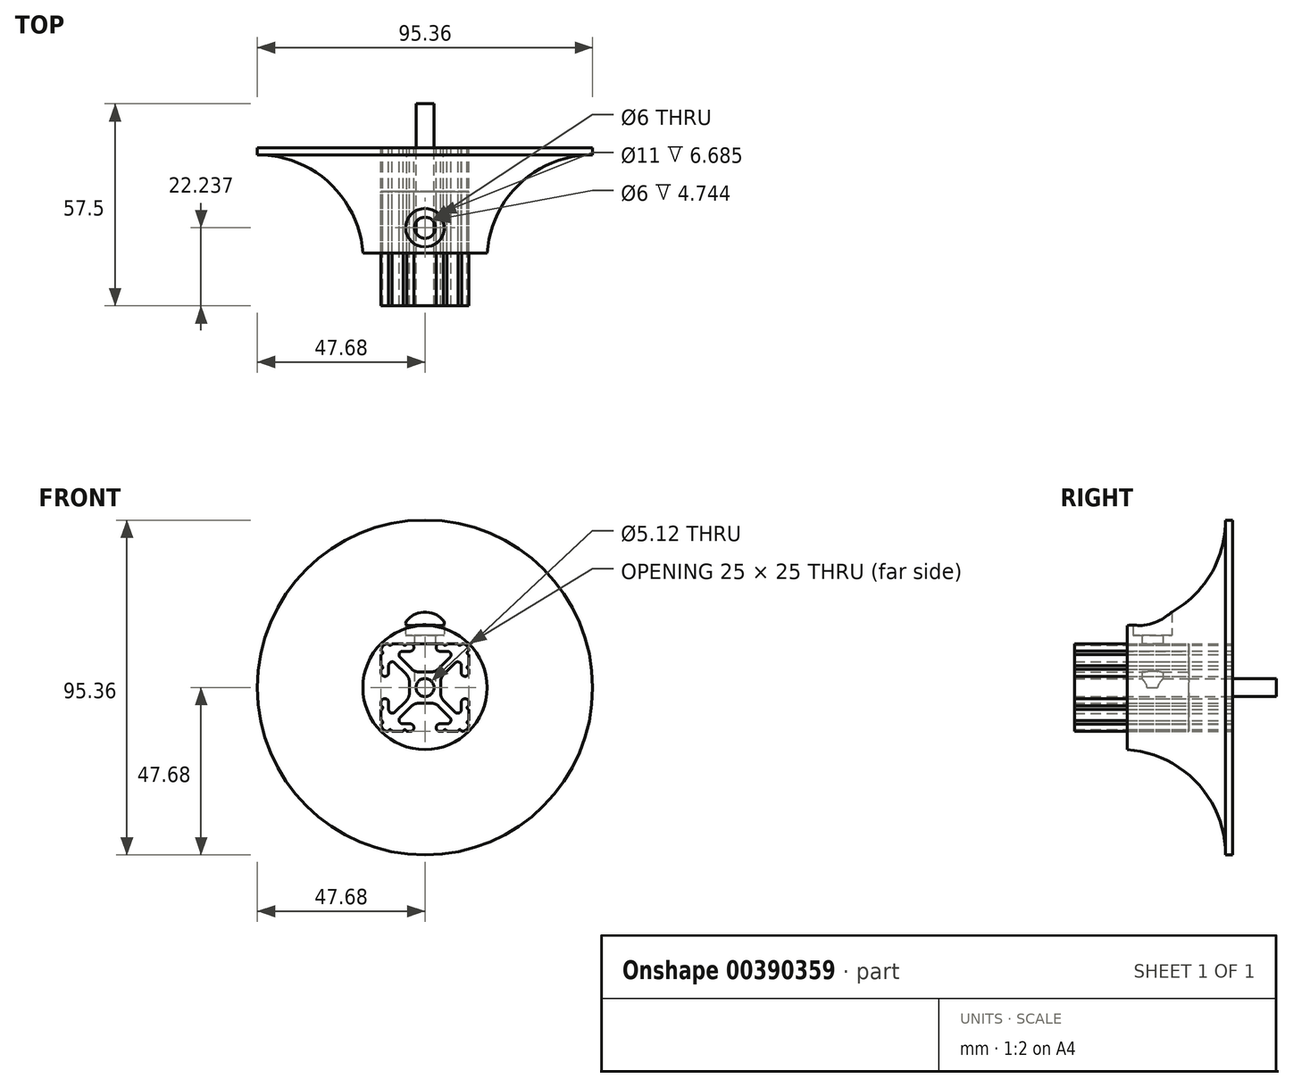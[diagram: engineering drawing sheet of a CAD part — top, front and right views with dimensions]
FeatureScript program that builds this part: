
annotation { "Feature Type Name" : "Feature", "Feature Type Description" : "" }
export const myFeature = defineFeature(function(context is Context, id is Id, definition is map)
    precondition{}
    {
        {
            var Q0;
            Q0=qCreatedBy(makeId("Front.planeOp"),FACE);
            var sketch = newSketch(context, id + "F0", { "sketchPlane" : qUnion([Q0])});
            skCircle(sketch, "E0", {"center": v(0, 0) * mm, "radius": 2.56 * mm});
            skArc(sketch, "E1", {"start": v(-1.68, -4.43) * mm, "mid": v(-2.88, -4.66) * mm, "end": v(-3.9, -5.34) * mm});
            skLineSegment(sketch, "E2", {"start": v(-1.68, -4.42) * mm, "end": v(1.68, -4.42) * mm});
            skArc(sketch, "E3", {"start": v(3.9, -5.34) * mm, "mid": v(2.88, -4.66) * mm, "end": v(1.68, -4.43) * mm});
            skLineSegment(sketch, "E4", {"start": v(3.9, -5.34) * mm, "end": v(7.07, -8.5) * mm});
            skArc(sketch, "E5", {"start": v(6.32, -10.32) * mm, "mid": v(7.3, -9.67) * mm, "end": v(7.07, -8.5) * mm});
            skLineSegment(sketch, "E6", {"start": v(6.32, -10.33) * mm, "end": v(4.22, -10.33) * mm});
            skArc(sketch, "E7", {"start": v(4.22, -10.32) * mm, "mid": v(3.49, -10.63) * mm, "end": v(3.19, -11.36) * mm});
            skLineSegment(sketch, "E8", {"start": v(3.19, -11.36) * mm, "end": v(3.19, -11.47) * mm});
            skArc(sketch, "E9", {"start": v(3.19, -11.47) * mm, "mid": v(3.49, -12.2) * mm, "end": v(4.22, -12.5) * mm});
            skLineSegment(sketch, "E10", {"start": v(4.22, -12.5) * mm, "end": v(5.23, -12.5) * mm});
            skArc(sketch, "E11", {"start": v(6.23, -12.5) * mm, "mid": v(5.73, -12) * mm, "end": v(5.23, -12.5) * mm});
            skLineSegment(sketch, "E12", {"start": v(6.23, -12.5) * mm, "end": v(9.4, -12.5) * mm});
            skArc(sketch, "E13", {"start": v(10.4, -12.5) * mm, "mid": v(9.9, -12) * mm, "end": v(9.4, -12.5) * mm});
            skArc(sketch, "E14", {"start": v(10.4, -12.5) * mm, "mid": v(11.9, -11.9) * mm, "end": v(12.5, -10.4) * mm});
            skArc(sketch, "E15", {"start": v(12.5, -9.4) * mm, "mid": v(12, -9.9) * mm, "end": v(12.5, -10.4) * mm});
            skLineSegment(sketch, "E16", {"start": v(12.5, -9.4) * mm, "end": v(12.5, -6.23) * mm});
            skArc(sketch, "E17", {"start": v(12.5, -5.23) * mm, "mid": v(12, -5.73) * mm, "end": v(12.5, -6.23) * mm});
            skLineSegment(sketch, "E18", {"start": v(12.5, -5.23) * mm, "end": v(12.5, -4.22) * mm});
            skArc(sketch, "E19", {"start": v(12.5, -4.22) * mm, "mid": v(12.2, -3.49) * mm, "end": v(11.47, -3.19) * mm});
            skLineSegment(sketch, "E20", {"start": v(11.47, -3.19) * mm, "end": v(11.36, -3.19) * mm});
            skArc(sketch, "E21", {"start": v(11.36, -3.19) * mm, "mid": v(10.63, -3.49) * mm, "end": v(10.32, -4.22) * mm});
            skLineSegment(sketch, "E22", {"start": v(10.33, -4.22) * mm, "end": v(10.33, -6.3) * mm});
            skArc(sketch, "E23", {"start": v(8.6, -7.02) * mm, "mid": v(9.7, -7.24) * mm, "end": v(10.33, -6.3) * mm});
            skLineSegment(sketch, "E24", {"start": v(8.6, -7.02) * mm, "end": v(5.36, -3.78) * mm});
            skArc(sketch, "E25", {"start": v(4.44, -1.57) * mm, "mid": v(4.68, -2.77) * mm, "end": v(5.36, -3.78) * mm});
            skLineSegment(sketch, "E26", {"start": v(4.44, -1.57) * mm, "end": v(4.44, 1.57) * mm});
            skArc(sketch, "E27", {"start": v(5.36, 3.78) * mm, "mid": v(4.68, 2.77) * mm, "end": v(4.44, 1.57) * mm});
            skLineSegment(sketch, "E28", {"start": v(5.36, 3.78) * mm, "end": v(8.6, 7.02) * mm});
            skArc(sketch, "E29", {"start": v(10.33, 6.3) * mm, "mid": v(9.7, 7.24) * mm, "end": v(8.6, 7.02) * mm});
            skLineSegment(sketch, "E30", {"start": v(10.33, 6.3) * mm, "end": v(10.33, 4.22) * mm});
            skArc(sketch, "E31", {"start": v(10.32, 4.22) * mm, "mid": v(10.63, 3.49) * mm, "end": v(11.36, 3.19) * mm});
            skLineSegment(sketch, "E32", {"start": v(11.36, 3.19) * mm, "end": v(11.47, 3.19) * mm});
            skArc(sketch, "E33", {"start": v(11.47, 3.19) * mm, "mid": v(12.2, 3.49) * mm, "end": v(12.5, 4.22) * mm});
            skLineSegment(sketch, "E34", {"start": v(12.5, 4.22) * mm, "end": v(12.5, 5.23) * mm});
            skArc(sketch, "E35", {"start": v(12.5, 6.23) * mm, "mid": v(12, 5.73) * mm, "end": v(12.5, 5.23) * mm});
            skLineSegment(sketch, "E36", {"start": v(12.5, 6.23) * mm, "end": v(12.5, 9.4) * mm});
            skArc(sketch, "E37", {"start": v(12.5, 10.4) * mm, "mid": v(12, 9.9) * mm, "end": v(12.5, 9.4) * mm});
            skArc(sketch, "E38", {"start": v(12.5, 10.4) * mm, "mid": v(11.9, 11.9) * mm, "end": v(10.4, 12.5) * mm});
            skArc(sketch, "E39", {"start": v(9.4, 12.5) * mm, "mid": v(9.9, 12) * mm, "end": v(10.4, 12.5) * mm});
            skLineSegment(sketch, "E40", {"start": v(9.4, 12.5) * mm, "end": v(6.23, 12.5) * mm});
            skArc(sketch, "E41", {"start": v(5.23, 12.5) * mm, "mid": v(5.73, 12) * mm, "end": v(6.23, 12.5) * mm});
            skLineSegment(sketch, "E42", {"start": v(5.23, 12.5) * mm, "end": v(4.22, 12.5) * mm});
            skArc(sketch, "E43", {"start": v(4.22, 12.5) * mm, "mid": v(3.49, 12.2) * mm, "end": v(3.19, 11.47) * mm});
            skLineSegment(sketch, "E44", {"start": v(3.19, 11.47) * mm, "end": v(3.19, 11.36) * mm});
            skArc(sketch, "E45", {"start": v(3.19, 11.36) * mm, "mid": v(3.49, 10.63) * mm, "end": v(4.22, 10.32) * mm});
            skLineSegment(sketch, "E46", {"start": v(4.22, 10.33) * mm, "end": v(6.37, 10.33) * mm});
            skArc(sketch, "E47", {"start": v(7.1, 8.59) * mm, "mid": v(7.32, 9.7) * mm, "end": v(6.37, 10.32) * mm});
            skLineSegment(sketch, "E48", {"start": v(7.1, 8.59) * mm, "end": v(3.84, 5.34) * mm});
            skArc(sketch, "E49", {"start": v(1.63, 4.43) * mm, "mid": v(2.82, 4.66) * mm, "end": v(3.84, 5.34) * mm});
            skLineSegment(sketch, "E50", {"start": v(1.63, 4.42) * mm, "end": v(-1.63, 4.42) * mm});
            skArc(sketch, "E51", {"start": v(-3.84, 5.34) * mm, "mid": v(-2.82, 4.66) * mm, "end": v(-1.63, 4.43) * mm});
            skLineSegment(sketch, "E52", {"start": v(-3.84, 5.34) * mm, "end": v(-7.1, 8.59) * mm});
            skArc(sketch, "E53", {"start": v(-6.37, 10.32) * mm, "mid": v(-7.32, 9.7) * mm, "end": v(-7.1, 8.59) * mm});
            skLineSegment(sketch, "E54", {"start": v(-6.37, 10.33) * mm, "end": v(-4.22, 10.33) * mm});
            skArc(sketch, "E55", {"start": v(-4.22, 10.32) * mm, "mid": v(-3.49, 10.63) * mm, "end": v(-3.19, 11.36) * mm});
            skLineSegment(sketch, "E56", {"start": v(-3.19, 11.36) * mm, "end": v(-3.19, 11.47) * mm});
            skArc(sketch, "E57", {"start": v(-3.19, 11.47) * mm, "mid": v(-3.49, 12.2) * mm, "end": v(-4.22, 12.5) * mm});
            skLineSegment(sketch, "E58", {"start": v(-4.22, 12.5) * mm, "end": v(-5.23, 12.5) * mm});
            skArc(sketch, "E59", {"start": v(-6.23, 12.5) * mm, "mid": v(-5.73, 12) * mm, "end": v(-5.23, 12.5) * mm});
            skLineSegment(sketch, "E60", {"start": v(-6.23, 12.5) * mm, "end": v(-9.4, 12.5) * mm});
            skArc(sketch, "E61", {"start": v(-10.4, 12.5) * mm, "mid": v(-9.9, 12) * mm, "end": v(-9.4, 12.5) * mm});
            skArc(sketch, "E62", {"start": v(-10.4, 12.5) * mm, "mid": v(-11.9, 11.9) * mm, "end": v(-12.5, 10.4) * mm});
            skArc(sketch, "E63", {"start": v(-12.5, 9.4) * mm, "mid": v(-12, 9.9) * mm, "end": v(-12.5, 10.4) * mm});
            skLineSegment(sketch, "E64", {"start": v(-12.5, 9.4) * mm, "end": v(-12.5, 6.23) * mm});
            skArc(sketch, "E65", {"start": v(-12.5, 5.23) * mm, "mid": v(-12, 5.73) * mm, "end": v(-12.5, 6.23) * mm});
            skLineSegment(sketch, "E66", {"start": v(-12.5, 5.23) * mm, "end": v(-12.5, 4.22) * mm});
            skArc(sketch, "E67", {"start": v(-12.5, 4.22) * mm, "mid": v(-12.2, 3.49) * mm, "end": v(-11.47, 3.19) * mm});
            skLineSegment(sketch, "E68", {"start": v(-11.47, 3.19) * mm, "end": v(-11.36, 3.19) * mm});
            skArc(sketch, "E69", {"start": v(-11.36, 3.19) * mm, "mid": v(-10.63, 3.49) * mm, "end": v(-10.32, 4.22) * mm});
            skLineSegment(sketch, "E70", {"start": v(-10.33, 4.22) * mm, "end": v(-10.33, 6.3) * mm});
            skArc(sketch, "E71", {"start": v(-8.6, 7.02) * mm, "mid": v(-9.7, 7.24) * mm, "end": v(-10.33, 6.3) * mm});
            skLineSegment(sketch, "E72", {"start": v(-8.6, 7.02) * mm, "end": v(-5.36, 3.78) * mm});
            skArc(sketch, "E73", {"start": v(-4.44, 1.57) * mm, "mid": v(-4.68, 2.77) * mm, "end": v(-5.36, 3.78) * mm});
            skLineSegment(sketch, "E74", {"start": v(-4.44, 1.57) * mm, "end": v(-4.44, -1.57) * mm});
            skArc(sketch, "E75", {"start": v(-5.36, -3.78) * mm, "mid": v(-4.68, -2.77) * mm, "end": v(-4.44, -1.57) * mm});
            skLineSegment(sketch, "E76", {"start": v(-5.36, -3.78) * mm, "end": v(-8.6, -7.02) * mm});
            skArc(sketch, "E77", {"start": v(-10.33, -6.3) * mm, "mid": v(-9.7, -7.24) * mm, "end": v(-8.6, -7.02) * mm});
            skLineSegment(sketch, "E78", {"start": v(-10.33, -6.3) * mm, "end": v(-10.33, -4.22) * mm});
            skArc(sketch, "E79", {"start": v(-10.32, -4.22) * mm, "mid": v(-10.63, -3.49) * mm, "end": v(-11.36, -3.19) * mm});
            skLineSegment(sketch, "E80", {"start": v(-11.36, -3.19) * mm, "end": v(-11.47, -3.19) * mm});
            skArc(sketch, "E81", {"start": v(-11.47, -3.19) * mm, "mid": v(-12.2, -3.49) * mm, "end": v(-12.5, -4.22) * mm});
            skLineSegment(sketch, "E82", {"start": v(-12.5, -4.22) * mm, "end": v(-12.5, -5.23) * mm});
            skArc(sketch, "E83", {"start": v(-12.5, -6.23) * mm, "mid": v(-12, -5.73) * mm, "end": v(-12.5, -5.23) * mm});
            skLineSegment(sketch, "E84", {"start": v(-12.5, -6.23) * mm, "end": v(-12.5, -9.4) * mm});
            skArc(sketch, "E85", {"start": v(-12.5, -10.4) * mm, "mid": v(-12, -9.9) * mm, "end": v(-12.5, -9.4) * mm});
            skArc(sketch, "E86", {"start": v(-12.5, -10.4) * mm, "mid": v(-11.9, -11.9) * mm, "end": v(-10.4, -12.5) * mm});
            skArc(sketch, "E87", {"start": v(-9.4, -12.5) * mm, "mid": v(-9.9, -12) * mm, "end": v(-10.4, -12.5) * mm});
            skLineSegment(sketch, "E88", {"start": v(-9.4, -12.5) * mm, "end": v(-6.23, -12.5) * mm});
            skArc(sketch, "E89", {"start": v(-5.23, -12.5) * mm, "mid": v(-5.73, -12) * mm, "end": v(-6.23, -12.5) * mm});
            skLineSegment(sketch, "E90", {"start": v(-5.23, -12.5) * mm, "end": v(-4.22, -12.5) * mm});
            skArc(sketch, "E91", {"start": v(-4.22, -12.5) * mm, "mid": v(-3.49, -12.2) * mm, "end": v(-3.19, -11.47) * mm});
            skLineSegment(sketch, "E92", {"start": v(-3.19, -11.47) * mm, "end": v(-3.19, -11.36) * mm});
            skArc(sketch, "E93", {"start": v(-3.19, -11.36) * mm, "mid": v(-3.49, -10.63) * mm, "end": v(-4.22, -10.32) * mm});
            skLineSegment(sketch, "E94", {"start": v(-4.22, -10.33) * mm, "end": v(-6.32, -10.33) * mm});
            skArc(sketch, "E95", {"start": v(-7.07, -8.5) * mm, "mid": v(-7.3, -9.67) * mm, "end": v(-6.32, -10.32) * mm});
            skLineSegment(sketch, "E96", {"start": v(-7.07, -8.5) * mm, "end": v(-3.9, -5.34) * mm});
            skSolve(sketch);
        }
        {
            var Q0;
            Q0=qCreatedBy(makeId("Front.planeOp"),FACE);
            var sketch = newSketch(context, id + "F1", { "sketchPlane" : qUnion([Q0])});
            skCircle(sketch, "E97", {"center": v(0, 0) * mm, "radius": 17.68 * mm});
            skCircle(sketch, "E98", {"center": v(0, 0) * mm, "radius": 47.67 * mm});
            skSolve(sketch);
        }
        {
            var Q0;
            Q0=qSketchRegion(id+"F1",true);
            var Q1;
            Q1=makeQuery(id+"F1.imprint","IMPRINT",FACE,{"disambiguationData":[TD([[makeQuery(id+"F1.imprint","IMPRINT",EDGE,{"derivedFrom":sQuery(id+"F1.wireOp",EDGE,"E97")}),1.0]])]});
            extrude(context, id + "F2", {"entities" : qUnion([Q0, Q1]), "depth" : 2 * mm});
        }
        {
            var Q0;
            Q0=makeQuery(id+"F1.imprint","IMPRINT",FACE,{"disambiguationData":[TD([[makeQuery(id+"F1.imprint","IMPRINT",EDGE,{"derivedFrom":sQuery(id+"F1.wireOp",EDGE,"E97")}),1.0]])]});
            extrude(context, id + "F3", {"entities" : qUnion([Q0]), "operationType" : NewBodyOperationType.ADD, "depth" : 30 * mm});
        }
        {
            var Q0;
            Q0=makeQuery(id+"F3.boolean.opBoolean","INTERSECT",EDGE,{"derivedFrom":[makeQuery(id+"F2.opExtrude","CAP_FACE",FACE,{"disambiguationData":[OSD([sQuery(id+"F1.wireOp",EDGE,"E98")])],"isStart":false}),makeQuery(id+"F3.opExtrude","SWEPT_FACE",FACE,{"disambiguationData":[OSD([sQuery(id+"F1.wireOp",EDGE,"E97")])]})]});
            fillet(context, id + "F4", {"entities" : qUnion([Q0]), "radius" : 30 * mm, "tangentPropagation" : true, "allowEdgeOverflow" : false});
        }
        {
            var Q0;
            Q0=makeQuery(id+"F1.imprint","IMPRINT",FACE,{"disambiguationData":[TD([[makeQuery(id+"F1.imprint","IMPRINT",EDGE,{"derivedFrom":sQuery(id+"F1.wireOp",EDGE,"E97")}),-1.0]])]});
            var sketch = newSketch(context, id + "F5", { "sketchPlane" : qUnion([Q0])});
            skArc(sketch, "E99.0.0", {"start": v(-6.32, -10.32) * mm, "mid": v(-7.3, -9.67) * mm, "end": v(-7.07, -8.5) * mm});
            skLineSegment(sketch, "E99.0.1", {"start": v(-7.07, -8.5) * mm, "end": v(-3.9, -5.34) * mm});
            skArc(sketch, "E99.0.2", {"start": v(-3.9, -5.34) * mm, "mid": v(-2.88, -4.66) * mm, "end": v(-1.68, -4.43) * mm});
            skLineSegment(sketch, "E99.0.3", {"start": v(-1.68, -4.42) * mm, "end": v(1.68, -4.42) * mm});
            skArc(sketch, "E99.0.4", {"start": v(1.68, -4.43) * mm, "mid": v(2.88, -4.66) * mm, "end": v(3.9, -5.34) * mm});
            skLineSegment(sketch, "E99.0.5", {"start": v(3.9, -5.34) * mm, "end": v(7.07, -8.5) * mm});
            skArc(sketch, "E99.0.6", {"start": v(7.07, -8.5) * mm, "mid": v(7.3, -9.67) * mm, "end": v(6.32, -10.33) * mm});
            skLineSegment(sketch, "E99.0.7", {"start": v(6.32, -10.33) * mm, "end": v(4.22, -10.33) * mm});
            skArc(sketch, "E99.0.8", {"start": v(4.22, -10.32) * mm, "mid": v(3.49, -10.63) * mm, "end": v(3.19, -11.36) * mm});
            skLineSegment(sketch, "E99.0.9", {"start": v(3.19, -11.36) * mm, "end": v(3.19, -11.47) * mm});
            skArc(sketch, "E99.0.10", {"start": v(3.19, -11.47) * mm, "mid": v(3.49, -12.2) * mm, "end": v(4.22, -12.5) * mm});
            skLineSegment(sketch, "E99.0.11", {"start": v(4.22, -12.5) * mm, "end": v(5.23, -12.5) * mm});
            skArc(sketch, "E99.0.12", {"start": v(5.23, -12.5) * mm, "mid": v(5.73, -12) * mm, "end": v(6.23, -12.5) * mm});
            skLineSegment(sketch, "E99.0.13", {"start": v(6.23, -12.5) * mm, "end": v(9.4, -12.5) * mm});
            skArc(sketch, "E99.0.14", {"start": v(9.4, -12.5) * mm, "mid": v(9.9, -12) * mm, "end": v(10.4, -12.5) * mm});
            skArc(sketch, "E99.0.15", {"start": v(10.4, -12.5) * mm, "mid": v(11.9, -11.9) * mm, "end": v(12.5, -10.4) * mm});
            skArc(sketch, "E99.0.16", {"start": v(12.5, -10.4) * mm, "mid": v(12, -9.9) * mm, "end": v(12.5, -9.4) * mm});
            skLineSegment(sketch, "E99.0.17", {"start": v(12.5, -9.4) * mm, "end": v(12.5, -6.23) * mm});
            skArc(sketch, "E99.0.18", {"start": v(12.5, -6.23) * mm, "mid": v(12, -5.73) * mm, "end": v(12.5, -5.23) * mm});
            skLineSegment(sketch, "E99.0.19", {"start": v(12.5, -5.23) * mm, "end": v(12.5, -4.22) * mm});
            skArc(sketch, "E99.0.20", {"start": v(12.5, -4.22) * mm, "mid": v(12.2, -3.49) * mm, "end": v(11.47, -3.19) * mm});
            skLineSegment(sketch, "E99.0.21", {"start": v(11.47, -3.19) * mm, "end": v(11.36, -3.19) * mm});
            skArc(sketch, "E99.0.22", {"start": v(11.36, -3.19) * mm, "mid": v(10.63, -3.49) * mm, "end": v(10.32, -4.22) * mm});
            skLineSegment(sketch, "E99.0.23", {"start": v(10.33, -4.22) * mm, "end": v(10.33, -6.3) * mm});
            skArc(sketch, "E99.0.24", {"start": v(10.33, -6.3) * mm, "mid": v(9.7, -7.24) * mm, "end": v(8.6, -7.02) * mm});
            skLineSegment(sketch, "E99.0.25", {"start": v(8.6, -7.02) * mm, "end": v(5.36, -3.78) * mm});
            skArc(sketch, "E99.0.26", {"start": v(5.36, -3.78) * mm, "mid": v(4.68, -2.77) * mm, "end": v(4.44, -1.57) * mm});
            skLineSegment(sketch, "E99.0.27", {"start": v(4.44, -1.57) * mm, "end": v(4.44, 1.57) * mm});
            skArc(sketch, "E99.0.28", {"start": v(4.44, 1.57) * mm, "mid": v(4.68, 2.77) * mm, "end": v(5.36, 3.78) * mm});
            skLineSegment(sketch, "E99.0.29", {"start": v(5.36, 3.78) * mm, "end": v(8.6, 7.02) * mm});
            skArc(sketch, "E99.0.30", {"start": v(8.6, 7.02) * mm, "mid": v(9.7, 7.24) * mm, "end": v(10.33, 6.3) * mm});
            skLineSegment(sketch, "E99.0.31", {"start": v(10.33, 6.3) * mm, "end": v(10.33, 4.22) * mm});
            skArc(sketch, "E99.0.32", {"start": v(10.32, 4.22) * mm, "mid": v(10.63, 3.49) * mm, "end": v(11.36, 3.19) * mm});
            skLineSegment(sketch, "E99.0.33", {"start": v(11.36, 3.19) * mm, "end": v(11.47, 3.19) * mm});
            skArc(sketch, "E99.0.34", {"start": v(11.47, 3.19) * mm, "mid": v(12.2, 3.49) * mm, "end": v(12.5, 4.22) * mm});
            skLineSegment(sketch, "E99.0.35", {"start": v(12.5, 4.22) * mm, "end": v(12.5, 5.23) * mm});
            skArc(sketch, "E99.0.36", {"start": v(12.5, 5.23) * mm, "mid": v(12, 5.73) * mm, "end": v(12.5, 6.23) * mm});
            skLineSegment(sketch, "E99.0.37", {"start": v(12.5, 6.23) * mm, "end": v(12.5, 9.4) * mm});
            skArc(sketch, "E99.0.38", {"start": v(12.5, 9.4) * mm, "mid": v(12, 9.9) * mm, "end": v(12.5, 10.4) * mm});
            skArc(sketch, "E99.0.39", {"start": v(12.5, 10.4) * mm, "mid": v(11.9, 11.9) * mm, "end": v(10.4, 12.5) * mm});
            skArc(sketch, "E99.0.40", {"start": v(10.4, 12.5) * mm, "mid": v(9.9, 12) * mm, "end": v(9.4, 12.5) * mm});
            skLineSegment(sketch, "E99.0.41", {"start": v(9.4, 12.5) * mm, "end": v(6.23, 12.5) * mm});
            skArc(sketch, "E99.0.42", {"start": v(6.23, 12.5) * mm, "mid": v(5.73, 12) * mm, "end": v(5.23, 12.5) * mm});
            skLineSegment(sketch, "E99.0.43", {"start": v(5.23, 12.5) * mm, "end": v(4.22, 12.5) * mm});
            skArc(sketch, "E99.0.44", {"start": v(4.22, 12.5) * mm, "mid": v(3.49, 12.2) * mm, "end": v(3.19, 11.47) * mm});
            skLineSegment(sketch, "E99.0.45", {"start": v(3.19, 11.47) * mm, "end": v(3.19, 11.36) * mm});
            skArc(sketch, "E99.0.46", {"start": v(3.19, 11.36) * mm, "mid": v(3.49, 10.63) * mm, "end": v(4.22, 10.32) * mm});
            skLineSegment(sketch, "E99.0.47", {"start": v(4.22, 10.33) * mm, "end": v(6.37, 10.33) * mm});
            skArc(sketch, "E99.0.48", {"start": v(6.37, 10.32) * mm, "mid": v(7.32, 9.7) * mm, "end": v(7.1, 8.59) * mm});
            skLineSegment(sketch, "E99.0.49", {"start": v(7.1, 8.59) * mm, "end": v(3.84, 5.34) * mm});
            skArc(sketch, "E99.0.50", {"start": v(3.84, 5.34) * mm, "mid": v(2.82, 4.66) * mm, "end": v(1.63, 4.43) * mm});
            skLineSegment(sketch, "E99.0.51", {"start": v(1.63, 4.42) * mm, "end": v(-1.63, 4.42) * mm});
            skArc(sketch, "E99.0.52", {"start": v(-1.63, 4.43) * mm, "mid": v(-2.82, 4.66) * mm, "end": v(-3.84, 5.34) * mm});
            skLineSegment(sketch, "E99.0.53", {"start": v(-3.84, 5.34) * mm, "end": v(-7.1, 8.59) * mm});
            skArc(sketch, "E99.0.54", {"start": v(-7.1, 8.59) * mm, "mid": v(-7.32, 9.7) * mm, "end": v(-6.37, 10.32) * mm});
            skLineSegment(sketch, "E99.0.55", {"start": v(-6.37, 10.33) * mm, "end": v(-4.22, 10.33) * mm});
            skArc(sketch, "E99.0.56", {"start": v(-4.22, 10.32) * mm, "mid": v(-3.49, 10.63) * mm, "end": v(-3.19, 11.36) * mm});
            skLineSegment(sketch, "E99.0.57", {"start": v(-3.19, 11.36) * mm, "end": v(-3.19, 11.47) * mm});
            skArc(sketch, "E99.0.58", {"start": v(-3.19, 11.47) * mm, "mid": v(-3.49, 12.2) * mm, "end": v(-4.22, 12.5) * mm});
            skLineSegment(sketch, "E99.0.59", {"start": v(-4.22, 12.5) * mm, "end": v(-5.23, 12.5) * mm});
            skArc(sketch, "E99.0.60", {"start": v(-5.23, 12.5) * mm, "mid": v(-5.73, 12) * mm, "end": v(-6.23, 12.5) * mm});
            skLineSegment(sketch, "E99.0.61", {"start": v(-6.23, 12.5) * mm, "end": v(-9.4, 12.5) * mm});
            skArc(sketch, "E99.0.62", {"start": v(-9.4, 12.5) * mm, "mid": v(-9.9, 12) * mm, "end": v(-10.4, 12.5) * mm});
            skArc(sketch, "E99.0.63", {"start": v(-10.4, 12.5) * mm, "mid": v(-11.9, 11.9) * mm, "end": v(-12.5, 10.4) * mm});
            skArc(sketch, "E99.0.64", {"start": v(-12.5, 10.4) * mm, "mid": v(-12, 9.9) * mm, "end": v(-12.5, 9.4) * mm});
            skLineSegment(sketch, "E99.0.65", {"start": v(-12.5, 9.4) * mm, "end": v(-12.5, 6.23) * mm});
            skArc(sketch, "E99.0.66", {"start": v(-12.5, 6.23) * mm, "mid": v(-12, 5.73) * mm, "end": v(-12.5, 5.23) * mm});
            skLineSegment(sketch, "E99.0.67", {"start": v(-12.5, 5.23) * mm, "end": v(-12.5, 4.22) * mm});
            skArc(sketch, "E99.0.68", {"start": v(-12.5, 4.22) * mm, "mid": v(-12.2, 3.49) * mm, "end": v(-11.47, 3.19) * mm});
            skLineSegment(sketch, "E99.0.69", {"start": v(-11.47, 3.19) * mm, "end": v(-11.36, 3.19) * mm});
            skArc(sketch, "E99.0.70", {"start": v(-11.36, 3.19) * mm, "mid": v(-10.63, 3.49) * mm, "end": v(-10.32, 4.22) * mm});
            skLineSegment(sketch, "E99.0.71", {"start": v(-10.33, 4.22) * mm, "end": v(-10.33, 6.3) * mm});
            skArc(sketch, "E99.0.72", {"start": v(-10.33, 6.3) * mm, "mid": v(-9.7, 7.24) * mm, "end": v(-8.6, 7.02) * mm});
            skLineSegment(sketch, "E99.0.73", {"start": v(-8.6, 7.02) * mm, "end": v(-5.36, 3.78) * mm});
            skArc(sketch, "E99.0.74", {"start": v(-5.36, 3.78) * mm, "mid": v(-4.68, 2.77) * mm, "end": v(-4.44, 1.57) * mm});
            skLineSegment(sketch, "E99.0.75", {"start": v(-4.44, 1.57) * mm, "end": v(-4.44, -1.57) * mm});
            skArc(sketch, "E99.0.76", {"start": v(-4.44, -1.57) * mm, "mid": v(-4.68, -2.77) * mm, "end": v(-5.36, -3.78) * mm});
            skLineSegment(sketch, "E99.0.77", {"start": v(-5.36, -3.78) * mm, "end": v(-8.6, -7.02) * mm});
            skArc(sketch, "E99.0.78", {"start": v(-8.6, -7.02) * mm, "mid": v(-9.7, -7.24) * mm, "end": v(-10.33, -6.3) * mm});
            skLineSegment(sketch, "E99.0.79", {"start": v(-10.33, -6.3) * mm, "end": v(-10.33, -4.22) * mm});
            skArc(sketch, "E99.0.80", {"start": v(-10.32, -4.22) * mm, "mid": v(-10.63, -3.49) * mm, "end": v(-11.36, -3.19) * mm});
            skLineSegment(sketch, "E99.0.81", {"start": v(-11.36, -3.19) * mm, "end": v(-11.47, -3.19) * mm});
            skArc(sketch, "E99.0.82", {"start": v(-11.47, -3.19) * mm, "mid": v(-12.2, -3.49) * mm, "end": v(-12.5, -4.22) * mm});
            skLineSegment(sketch, "E99.0.83", {"start": v(-12.5, -4.22) * mm, "end": v(-12.5, -5.23) * mm});
            skArc(sketch, "E99.0.84", {"start": v(-12.5, -5.23) * mm, "mid": v(-12, -5.73) * mm, "end": v(-12.5, -6.23) * mm});
            skLineSegment(sketch, "E99.0.85", {"start": v(-12.5, -6.23) * mm, "end": v(-12.5, -9.4) * mm});
            skArc(sketch, "E99.0.86", {"start": v(-12.5, -9.4) * mm, "mid": v(-12, -9.9) * mm, "end": v(-12.5, -10.4) * mm});
            skArc(sketch, "E99.0.87", {"start": v(-12.5, -10.4) * mm, "mid": v(-11.9, -11.9) * mm, "end": v(-10.4, -12.5) * mm});
            skArc(sketch, "E99.0.88", {"start": v(-10.4, -12.5) * mm, "mid": v(-9.9, -12) * mm, "end": v(-9.4, -12.5) * mm});
            skLineSegment(sketch, "E99.0.89", {"start": v(-9.4, -12.5) * mm, "end": v(-6.23, -12.5) * mm});
            skArc(sketch, "E99.0.90", {"start": v(-6.23, -12.5) * mm, "mid": v(-5.73, -12) * mm, "end": v(-5.23, -12.5) * mm});
            skLineSegment(sketch, "E99.0.91", {"start": v(-5.23, -12.5) * mm, "end": v(-4.22, -12.5) * mm});
            skArc(sketch, "E99.0.92", {"start": v(-4.22, -12.5) * mm, "mid": v(-3.49, -12.2) * mm, "end": v(-3.19, -11.47) * mm});
            skLineSegment(sketch, "E99.0.93", {"start": v(-3.19, -11.47) * mm, "end": v(-3.19, -11.36) * mm});
            skArc(sketch, "E99.0.94", {"start": v(-3.19, -11.36) * mm, "mid": v(-3.49, -10.63) * mm, "end": v(-4.22, -10.32) * mm});
            skLineSegment(sketch, "E99.0.95", {"start": v(-4.22, -10.33) * mm, "end": v(-6.32, -10.33) * mm});
            skLineSegment(sketch, "E100", {"start": v(4.22, 12.5) * mm, "end": v(-4.22, 12.5) * mm});
            skSolve(sketch);
        }
        {
            var Q0;
            Q0=qSketchRegion(id+"F5",true);
            extrude(context, id + "F6", {"entities" : qUnion([Q0]), "operationType" : NewBodyOperationType.REMOVE, "depth" : 40 * mm});
        }
        {
            var Q0;
            Q0=qSketchRegion(id+"F0",true);
            extrude(context, id + "F7", {"entities" : qUnion([Q0]), "depth" : 45 * mm});
        }
        {
            var Q0;
            Q0=qCreatedBy(makeId("Top.planeOp"),FACE);
            var sketch = newSketch(context, id + "F8", { "sketchPlane" : qUnion([Q0])});
            skCircle(sketch, "E101", {"center": v(0, -22.76) * mm, "radius": 5.5 * mm});
            skCircle(sketch, "E102", {"center": v(0, -22.76) * mm, "radius": 3 * mm});
            skSolve(sketch);
        }
        {
            var Q0;
            Q0=makeQuery(id+"F8.imprint","IMPRINT",FACE,{"disambiguationData":[TD([[makeQuery(id+"F8.imprint","IMPRINT",EDGE,{"derivedFrom":sQuery(id+"F8.wireOp",EDGE,"E102")}),1.0]])]});
            extrude(context, id + "F9", {"entities" : qUnion([Q0]), "operationType" : NewBodyOperationType.REMOVE, "depth" : 40 * mm});
        }
        {
            var Q0;
            Q0=makeQuery(id+"F8.imprint","IMPRINT",FACE,{"disambiguationData":[TD([[makeQuery(id+"F8.imprint","IMPRINT",EDGE,{"derivedFrom":sQuery(id+"F8.wireOp",EDGE,"E101")}),1.0]])]});
            extrude(context, id + "F10", {"entities" : qUnion([Q0]), "operationType" : NewBodyOperationType.REMOVE, "depth" : 25 * mm, "hasSecondDirection" : true, "secondDirectionOppositeDirection" : false, "secondDirectionDepth" : 14.8 * mm});
        }
        {
            var Q0;
            Q0=makeQuery(id+"F0.imprint","IMPRINT",FACE,{"disambiguationData":[TD([[makeQuery(id+"F0.imprint","IMPRINT",EDGE,{"derivedFrom":sQuery(id+"F0.wireOp",EDGE,"E0")}),1.0]])]});
            extrude(context, id + "F11", {"entities" : qUnion([Q0]), "endBound" : BoundingType.SYMMETRIC, "depth" : 25 * mm});
        }
        {
            var Q0;
            Q0=qSketchRegion(id+"F1",true);
            var Q1;
            Q1=makeQuery(id+"F1.imprint","IMPRINT",FACE,{"disambiguationData":[TD([[makeQuery(id+"F1.imprint","IMPRINT",EDGE,{"derivedFrom":sQuery(id+"F1.wireOp",EDGE,"E97")}),1.0]])]});
            extrude(context, id + "F12", {"entities" : qUnion([Q0, Q1]), "endBound" : BoundingType.SYMMETRIC, "depth" : 5 * mm});
        }
        {
            var Q0;
            Q0=qSketchRegion(id+"F0",true);
            extrude(context, id + "F13", {"entities" : qUnion([Q0]), "operationType" : NewBodyOperationType.REMOVE, "endBound" : BoundingType.SYMMETRIC, "oppositeDirection" : true, "depth" : 25 * mm});
        }
        {
            var Q0;
            Q0=makeQuery(id+"F13.boolean.opBoolean","SPLIT",BODY,{"disambiguationData":[OD(1.0)],"derivedFrom":makeQuery(id+"F12.opExtrude","SWEPT_BODY",BODY,{"disambiguationData":[OSD([sQuery(id+"F1.wireOp",EDGE,"E98")])]})});
            deleteBodies(context, id + "F14", {"entities" : qUnion([Q0])});
        }
    });
